# Revit family: IS_CerathermT125_A7588_BIM_NL
name_source: partatom
category: Plumbing Fixtures
units: mm (PartAtom-declared; Revit-internal decimal feet)

## family parameters
Always vertical = No
Cut with Voids When Loaded = No
OmniClass Number = 23.45.55.17
OmniClass Title = Mixing Faucets
Part Type = Normal
Room Calculation Point = No
Round Connector Dimension = Use Diameter
Shared = No
Work Plane-Based = No

## types (4) — shared parameters
Accesoires = https://www.idealstandard.nl
Accessories = https://www.idealstandard.de
Afmetingen = 303 x 178 x 70 mm
AfstandsEenheid = Millimeter
AreaUnits = millimeters
AssetType = Plumbing Fittures
Auteur = Ideal Standard
BIMObjectName = IS_IdealStandard_Watersupplyfittingsforbaths_Ceratherm T125  _A7588
BIMobject category = Taps & Mixers
BIMobject category code = sanitary-taps-mixers
BIMobject main category = Sanitary
BIMobject main category code = sanitary
Beschrijvinggarantie = Herstellergarantie
BimObjectNaam = IS_IdealStandard_Watersupplyfittingsforbaths_Ceratherm T125  _A7588
Brand = Ideal Standard
Brand url = http://www.idealstandard.nl
Category = Plumbing Fixtures
Classification = Shower Mixers
ConnectionType = Plumbing
CurrencyUnit = €
CurrentRevision = 1
Date of publishing = 14/04/2022
Douchebak = No
DurationUnit = Years
DuurEenheid = bar
Edition number = 1
FaucetFunction = Manual Bath & Shower Mixer
FaucetOperation = Manual Shower Mixers
FaucetTopDescription = Manual Bath & Shower Mixer
Functiekraanwerk = Dusch- und Wannenmischer
GTIN code = https://4015413351720
Garantieunits = Jahre
GemaaktOp = 14/04/2022
Help = https://www.idealstandard.ee
Hoogte = 70.04898
Hulp = https://www.idealstandard.ee
IFC Classification = Sanitary Terminal
IfcExportAs = IfcValveType
IfcExportType = FAUCET
Installatieinstructies = https://www.idealstandard.nl
Installation instructions = https://www.idealstandard.nl
InstallationInstructions = https://www.idealstandard.nl
Lengte = 178 mm
LinearUnits = millimeters
MaintenanceInformation = https://www.idealstandard.nl
Manufacturer = Ideal Standard
Manufacturer name = Ideal Standard
ManufacturerURL = http://www.idealstandard.nl
Materiaal = Messing
Material = Messing
Material main = Messing
Merk = Ideal Standard
NBS Reference Code = 45-35-70/315
NBS Reference Description = Water supply fittings for baths
Name = Watersupplyfittingsforbaths_Ceratherm T125 _A7588_IdealStandard
NettWeight = 2.73
Nettogewicht = 2.73
NominalDepth = 178 mm
NominalHeight = 70 mm
NominalLength = 178 mm
NominalWidth = 303 mm
Normen = Watersupplyfittingsforbaths_Ceratherm T125 _A7588_IdealStandard
OppervlakteEenheid = Millimeter
Product Guid = 468085ce-ebd2-4ef1-b1cd-9c98ede7d66a
Product SKU = A7588
Product certification = https://www.idealstandard.de
Product data url = https://bimobject.com
Product family = CERATHERM
Product group = Taps & Mixers
Product name = CERATHERM T125 ESPOSED SHOWER AND BATH MIXER
Product url = https://www.idealstandard.nl
ProductInformation = https://www.idealstandard.nl
ProductSoort = Badewannen- und Brausebatterie
Productinformatie = https://www.idealstandard.nl
QR code = http://bimobject.com
Revisie = 1
Shape = cylindrical
ShowerType = Bath & Shower Mixer
Size = 303 x 178 x 70 mm
Space = internal
SpareParts = https://www.idealstandard.nl
Technical description = https://www.idealstandard.nl
Telefoonnummer = 077 355 08 08
TestPressure = 10 bar
Testdruk = 10 bar
Typeconnectie = Installation
Typekraanwerk = Dusch- und Wannenmischer
UNSPSC Code = 301815
URL = http://www.idealstandard.nl
Uniclass 1.4 Code = L725111
Uniclass 1.4 Description = Mixer Taps
Uniclass 2.0 Code = PR-35-06-07
Uniclass 2.0 Description = Bath Water Supply Fittings
Uniclass 2015 Code = Pr_40_20_87_08
Uniclass 2015 Name = Bath mixer taps
Uniclass2015Beschrijving = Bath mixer taps
Uniclass2015Code = Pr_40_20_87_08
Uniclass2015Referentie = Pr_40_20_87_08
Uniclass2015Title = Bath mixer taps
Uniclass2015Version = v1.25
Uniformat II Code = C1030
Uniformat II Description = Fittings
Urlproducent = https://www.idealstandard.nl
ValutaEenheid = Euro
Versie = 1
Version = 1
VolumeUnits = Litres
Volumeunits = Liter
Vorm = zylindrisch
WRASURL = https://www.wrasapprovals.co.uk
WarrantyDescription = Manufacturer warranty
WarrantyDurationParts = 5
WarrantyDurationUnit = years
Wisselstukken = https://www.idealstandard.nl
Youtube clip = https://www.youtube.com
zero-valued in all types: Breedte, BrutoGewicht, Diepte, MaterialThickness, Vervangingskosten

## per-type parameters (varying)
| type | Afwerking | Artikelnummer | Artikelomschrijving | Artikelreferentie | BarCode | Color | Description | Eigenschappen | Features | Finish | Kleur | MainColor | Model | ModelNumber | ModelReference | Referentie |
| A7588GN - CERATHERM T125 EXPOSED SHOWER AND BATH MIXER - SILVER STORM | Silberner Sturm | A7588GN | Ceratherm T125 Wannenthermostat Brausebatterie, Stiftgriff mit S-Anschluss - Silver Storm | CERATHERM T EXPOSED SHOWER AND BATH MIXER - SILVER STORM | 4015413354189 | Silver Storm | Ceratherm T125 thermostatic bath shower mixer, pin handle with S-Connector - Silver Storm | Wannen-Brause-Thermostatbatterie, Pin-Griff mit S-Anschluss - Silver Storm | Thermostatic bath shower mixer, pin handle with S-Connector - Silver Storm | Silver Storm | Silberner Sturm | Silver Storm | A7588GN | A7588GN | CERATHERM T EXPOSED SHOWER AND BATH MIXER - SILVER STORM | CERATHERM T EXPOSED SHOWER AND BATH MIXER - SILVER STORM |
| A7588AA - CERATHERM T125 EXPOSED SHOWER AND BATH MIXER - CHROME | Chrom | A7588AA | Ceratherm T125 Wannen-Brausen-Thermostat, Stiftgriff mit S-Anschluss - Chrom | CERATHERM T EXPOSED SHOWER AND BATH MIXER - CHROME | 4015413351720 | Chrome | Ceratherm T125 thermostatic bath shower mixer, pin handle with S-Connector - Chrome | Wannen-Brausethermostat, Pin-Griff mit S-Anschluss - Chrom | Thermostatic bath shower mixer, pin handle with S-Connector - Chrome | Chrome | Chrom | Chrome | A7588AA | A7588AA | CERATHERM T EXPOSED SHOWER AND BATH MIXER - CHROME | CERATHERM T EXPOSED SHOWER AND BATH MIXER - CHROME |
| A7588A5 - CERATHERM T125 EXPOSED SHOWER AND BATH MIXER - MAGNETIC GREY | Magnetisches Grau | A7588A5 | Ceratherm T125 Wannen-Brausen-Thermostat, Pin-Griff mit S-Anschluss - Magnetic Grey | CERATHERM T EXPOSED SHOWER AND BATH MIXER - MAGNETIC GREY | 4015413354172 | Magnetic Grey | Ceratherm T125 thermostatic bath shower mixer, pin handle with S-Connector - Magnetic Grey | Wannen-Brausen-Thermostatmischer, Pin-Griff mit S-Connector - Magnetic Grey | Thermostatic bath shower mixer, pin handle with S-Connector - Magnetic Grey | Magnetic Grey | Magnetisches Grau | Magnetic Grey | A7588A5 | A7588A5 | CERATHERM T EXPOSED SHOWER AND BATH MIXER - MAGNETIC GREY | CERATHERM T EXPOSED SHOWER AND BATH MIXER - MAGNETIC GREY |
| A7588A2 - CERATHERM T125 EXPOSED SHOWER AND BATH MIXER - BRUSH GOLD | Pinsel Gold | A7588A2 | Ceratherm T125 Wannen-Brausen-Thermostat, Pin-Griff mit S-Connector - Brush Gold | CERATHERM T EXPOSED SHOWER AND BATH MIXER - BRUSH GOLD | 4015413354165 | Brush Gold | Ceratherm T125 thermostatic bath shower mixer, pin handle with S-Connector - Brush Gold | Wannen-Brausemischer mit Thermostat, Pin-Griff mit S-Anschluss - Brush Gold | Thermostatic bath shower mixer, pin handle with S-Connector - Brush Gold | Brush Gold | Pinsel Gold | Brush Gold | A7588A2 | A7588A2 | CERATHERM T EXPOSED SHOWER AND BATH MIXER - BRUSH GOLD | CERATHERM T EXPOSED SHOWER AND BATH MIXER - BRUSH GOLD |

## geometry (parser evidence)
native form markers: Sweep x4
no freeform markers — native parametric forms only
